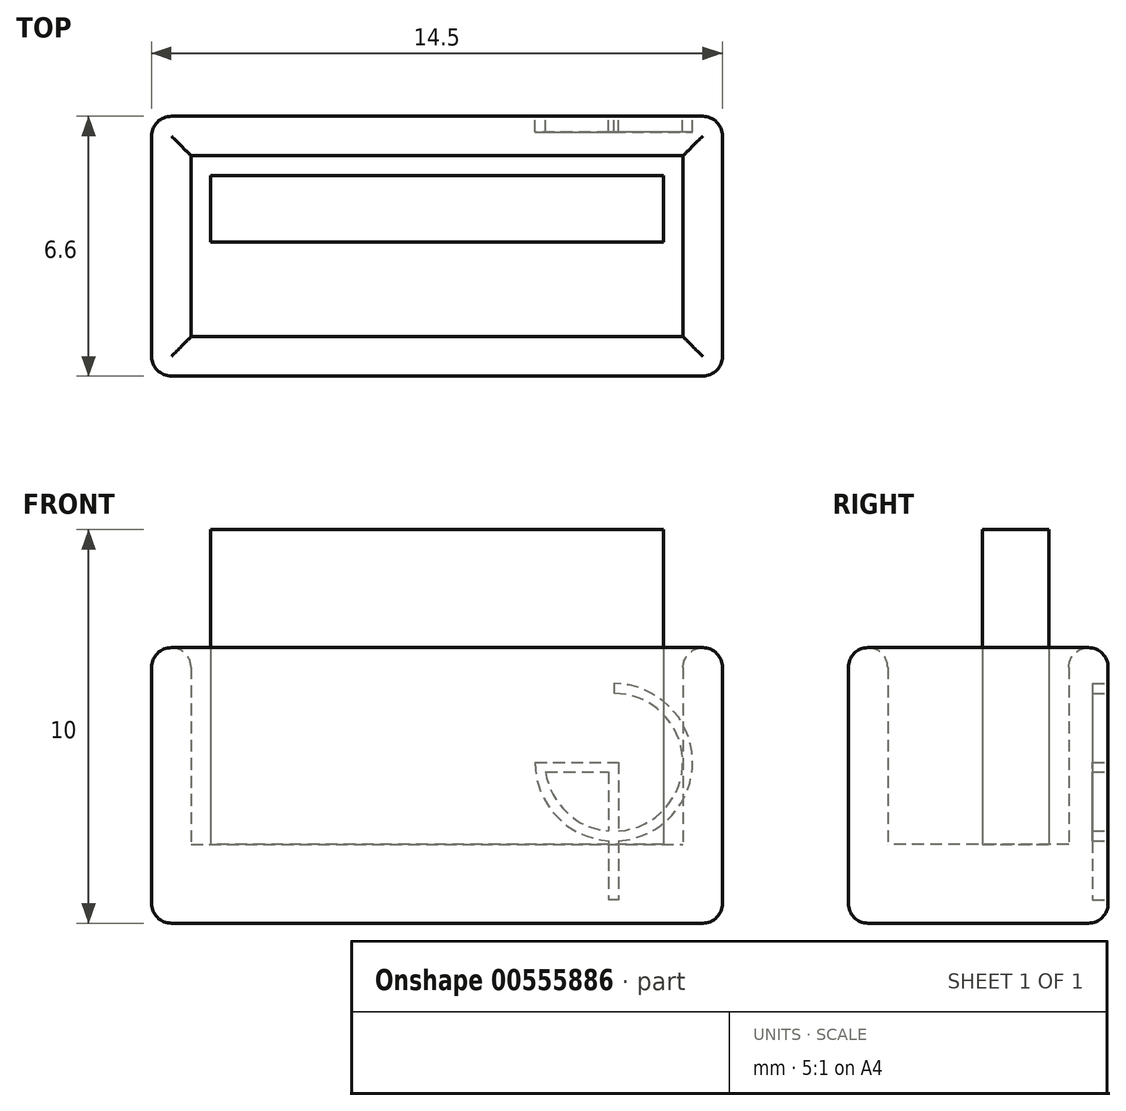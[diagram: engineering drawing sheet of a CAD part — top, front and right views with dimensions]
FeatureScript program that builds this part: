
annotation { "Feature Type Name" : "Feature", "Feature Type Description" : "" }
export const myFeature = defineFeature(function(context is Context, id is Id, definition is map)
    precondition{}
    {
        {
            var Q0;
            Q0=qCreatedBy(makeId("Top.planeOp"),FACE);
            var sketch = newSketch(context, id + "F0", { "sketchPlane" : qUnion([Q0])});
            skLineSegment(sketch, "E0.bottom", {"start": v(-5.64, 2.3) * mm, "end": v(6.86, 2.3) * mm});
            skLineSegment(sketch, "E0.top", {"start": v(-5.64, -2.3) * mm, "end": v(6.86, -2.3) * mm});
            skLineSegment(sketch, "E0.left", {"start": v(-5.64, 2.3) * mm, "end": v(-5.64, -2.3) * mm});
            skLineSegment(sketch, "E0.right", {"start": v(6.86, 2.3) * mm, "end": v(6.86, -2.3) * mm});
            skLineSegment(sketch, "E1.0", {"start": v(-6.64, -3.3) * mm, "end": v(7.86, -3.3) * mm});
            skLineSegment(sketch, "E1.1", {"start": v(-6.64, 3.3) * mm, "end": v(-6.64, -3.3) * mm});
            skLineSegment(sketch, "E1.2", {"start": v(-6.64, 3.3) * mm, "end": v(7.86, 3.3) * mm});
            skLineSegment(sketch, "E1.3", {"start": v(7.86, 3.3) * mm, "end": v(7.86, -3.3) * mm});
            skLineSegment(sketch, "E2.bottom", {"start": v(-5.14, 1.8) * mm, "end": v(6.36, 1.8) * mm});
            skLineSegment(sketch, "E2.top", {"start": v(-5.14, 0.1) * mm, "end": v(6.36, 0.1) * mm});
            skLineSegment(sketch, "E2.left", {"start": v(-5.14, 1.8) * mm, "end": v(-5.14, 0.1) * mm});
            skLineSegment(sketch, "E2.right", {"start": v(6.36, 1.8) * mm, "end": v(6.36, 0.1) * mm});
            skSolve(sketch);
        }
        {
            var Q0;
            Q0 = qSketchRegion(id + "F0", true);
            extrude(context, id + "F1", {"entities" : qUnion([Q0]), "depth" : 7 * mm, "offsetDistance" : 25 * mm});
        }
        {
            var Q0;
            {var subQ0=sQuery(id+"F0.wireOp",EDGE,"E0.top");Q0=makeQuery(id+"F0.imprint","IMPRINT",FACE,{"disambiguationData":[TD([[makeQuery(id+"F0.imprint","IMPRINT",EDGE,{"derivedFrom":subQ0}),1.0]])]});}
            var Q1;
            {var subQ0=sQuery(id+"F0.wireOp",EDGE,"E0.bottom");Q1=makeQuery(id+"F0.imprint","IMPRINT",FACE,{"disambiguationData":[TD([[makeQuery(id+"F0.imprint","IMPRINT",EDGE,{"derivedFrom":subQ0}),-1.0]])]});}
            var Q2;
            Q2=makeQuery(id+"F0.imprint","IMPRINT",FACE,{"disambiguationData":[TD([[makeQuery(id+"F0.imprint","IMPRINT",EDGE,{"derivedFrom":sQuery(id+"F0.wireOp",EDGE,"E2.bottom")}),-1.0]])]});
            extrude(context, id + "F2", {"entities" : qUnion([Q0, Q1, Q2]), "operationType" : NewBodyOperationType.ADD, "depth" : 2 * mm, "offsetDistance" : 25 * mm});
        }
        {
            var Q0;
            Q0=makeQuery(id+"F0.imprint","IMPRINT",FACE,{"disambiguationData":[TD([[makeQuery(id+"F0.imprint","IMPRINT",EDGE,{"derivedFrom":sQuery(id+"F0.wireOp",EDGE,"E2.bottom")}),-1.0]])]});
            extrude(context, id + "F3", {"entities" : qUnion([Q0]), "operationType" : NewBodyOperationType.ADD, "depth" : 10 * mm, "offsetDistance" : 25 * mm});
        }
        {
            var Q0;
            Q0=makeQuery(id+"F1.opExtrude","SWEPT_FACE",FACE,{"disambiguationData":[OSD([sQuery(id+"F0.wireOp",EDGE,"E1.2")])]});
            var sketch = newSketch(context, id + "F4", { "sketchPlane" : qUnion([Q0])});
            skLineSegment(sketch, "E3.bottom", {"start": v(-5.1, 6.09) * mm, "end": v(-3.1, 6.09) * mm, "construction": true});
            skLineSegment(sketch, "E3.top", {"start": v(-5.1, 4.09) * mm, "end": v(-3.1, 4.09) * mm, "construction": true});
            skLineSegment(sketch, "E3.left", {"start": v(-5.1, 6.09) * mm, "end": v(-5.1, 4.09) * mm, "construction": true});
            skLineSegment(sketch, "E3.right", {"start": v(-3.1, 6.09) * mm, "end": v(-3.1, 4.09) * mm, "construction": true});
            skArc(sketch, "E4", {"start": v(-5.1, 6.09) * mm, "mid": v(-6.52, 2.67) * mm, "end": v(-3.1, 4.09) * mm});
            skLineSegment(sketch, "E5", {"start": v(-5.1, 6.09) * mm, "end": v(-5.1, 5.84) * mm});
            skLineSegment(sketch, "E6", {"start": v(-3.1, 4.09) * mm, "end": v(-3.35, 4.09) * mm});
            skArc(sketch, "E7", {"start": v(-5.1, 5.84) * mm, "mid": v(-6.34, 2.85) * mm, "end": v(-3.35, 4.09) * mm});
            skLineSegment(sketch, "E8", {"start": v(-3.35, 4.09) * mm, "end": v(-5.22, 4.09) * mm});
            skLineSegment(sketch, "E9", {"start": v(-5.22, 4.09) * mm, "end": v(-5.22, 0.59) * mm});
            skLineSegment(sketch, "E10", {"start": v(-5.22, 0.59) * mm, "end": v(-4.97, 0.59) * mm});
            skLineSegment(sketch, "E11", {"start": v(-3.37, 3.84) * mm, "end": v(-4.97, 3.84) * mm});
            skLineSegment(sketch, "E12", {"start": v(-4.97, 3.84) * mm, "end": v(-4.97, 0.59) * mm});
            skSolve(sketch);
        }
        {
            var Q0;
            Q0 = qSketchRegion(id + "F4", true);
            extrude(context, id + "F5", {"entities" : qUnion([Q0]), "operationType" : NewBodyOperationType.REMOVE, "oppositeDirection" : true, "depth" : .4 * mm, "offsetDistance" : 25 * mm});
        }
        {
            var Q0;
            Q0=makeQuery(id+"F1.opExtrude","SWEPT_EDGE",EDGE,{"disambiguationData":[OSD([sQuery(id+"F0.wireOp",EDGE,"E1.2"),sQuery(id+"F0.wireOp",EDGE,"E1.3")])]});
            var Q1;
            Q1=makeQuery(id+"F1.opExtrude","CAP_EDGE",EDGE,{"disambiguationData":[OSD([sQuery(id+"F0.wireOp",EDGE,"E1.2")])],"isStart":false});
            var Q2;
            Q2=makeQuery(id+"F1.opExtrude","CAP_EDGE",EDGE,{"disambiguationData":[OSD([sQuery(id+"F0.wireOp",EDGE,"E1.2")])],"isStart":true});
            var Q3;
            Q3=makeQuery(id+"F1.opExtrude","CAP_EDGE",EDGE,{"disambiguationData":[OSD([sQuery(id+"F0.wireOp",EDGE,"E1.3")])],"isStart":true});
            var Q4;
            Q4=makeQuery(id+"F1.opExtrude","CAP_EDGE",EDGE,{"disambiguationData":[OSD([sQuery(id+"F0.wireOp",EDGE,"E1.3")])],"isStart":false});
            var Q5;
            Q5=makeQuery(id+"F1.opExtrude","SWEPT_EDGE",EDGE,{"disambiguationData":[OSD([sQuery(id+"F0.wireOp",EDGE,"E1.0"),sQuery(id+"F0.wireOp",EDGE,"E1.3")])]});
            var Q6;
            Q6=makeQuery(id+"F1.opExtrude","CAP_EDGE",EDGE,{"disambiguationData":[OSD([sQuery(id+"F0.wireOp",EDGE,"E1.0")])],"isStart":true});
            var Q7;
            Q7=makeQuery(id+"F1.opExtrude","CAP_EDGE",EDGE,{"disambiguationData":[OSD([sQuery(id+"F0.wireOp",EDGE,"E1.1")])],"isStart":true});
            var Q8;
            Q8=makeQuery(id+"F1.opExtrude","SWEPT_EDGE",EDGE,{"disambiguationData":[OSD([sQuery(id+"F0.wireOp",EDGE,"E1.1"),sQuery(id+"F0.wireOp",EDGE,"E1.2")])]});
            var Q9;
            Q9=makeQuery(id+"F1.opExtrude","SWEPT_EDGE",EDGE,{"disambiguationData":[OSD([sQuery(id+"F0.wireOp",EDGE,"E1.0"),sQuery(id+"F0.wireOp",EDGE,"E1.1")])]});
            var Q10;
            Q10=makeQuery(id+"F1.opExtrude","CAP_EDGE",EDGE,{"disambiguationData":[OSD([sQuery(id+"F0.wireOp",EDGE,"E1.0")])],"isStart":false});
            var Q11;
            Q11=makeQuery(id+"F1.opExtrude","CAP_EDGE",EDGE,{"disambiguationData":[OSD([sQuery(id+"F0.wireOp",EDGE,"E1.1")])],"isStart":false});
            var Q12;
            Q12=makeQuery(id+"F1.opExtrude","CAP_EDGE",EDGE,{"disambiguationData":[OSD([sQuery(id+"F0.wireOp",EDGE,"E0.bottom")])],"isStart":false});
            var Q13;
            Q13=makeQuery(id+"F1.opExtrude","CAP_EDGE",EDGE,{"disambiguationData":[OSD([sQuery(id+"F0.wireOp",EDGE,"E0.top")])],"isStart":false});
            var Q14;
            Q14=makeQuery(id+"F1.opExtrude","CAP_EDGE",EDGE,{"disambiguationData":[OSD([sQuery(id+"F0.wireOp",EDGE,"E0.left")])],"isStart":false});
            var Q15;
            Q15=makeQuery(id+"F1.opExtrude","CAP_EDGE",EDGE,{"disambiguationData":[OSD([sQuery(id+"F0.wireOp",EDGE,"E0.right")])],"isStart":false});
            fillet(context, id + "F6", {"entities" : qUnion([Q0, Q1, Q2, Q3, Q4, Q5, Q6, Q7, Q8, Q9, Q10, Q11, Q12, Q13, Q14, Q15]), "radius" : .5 * mm, "tangentPropagation" : true, "allowEdgeOverflow" : false});
        }
    });
